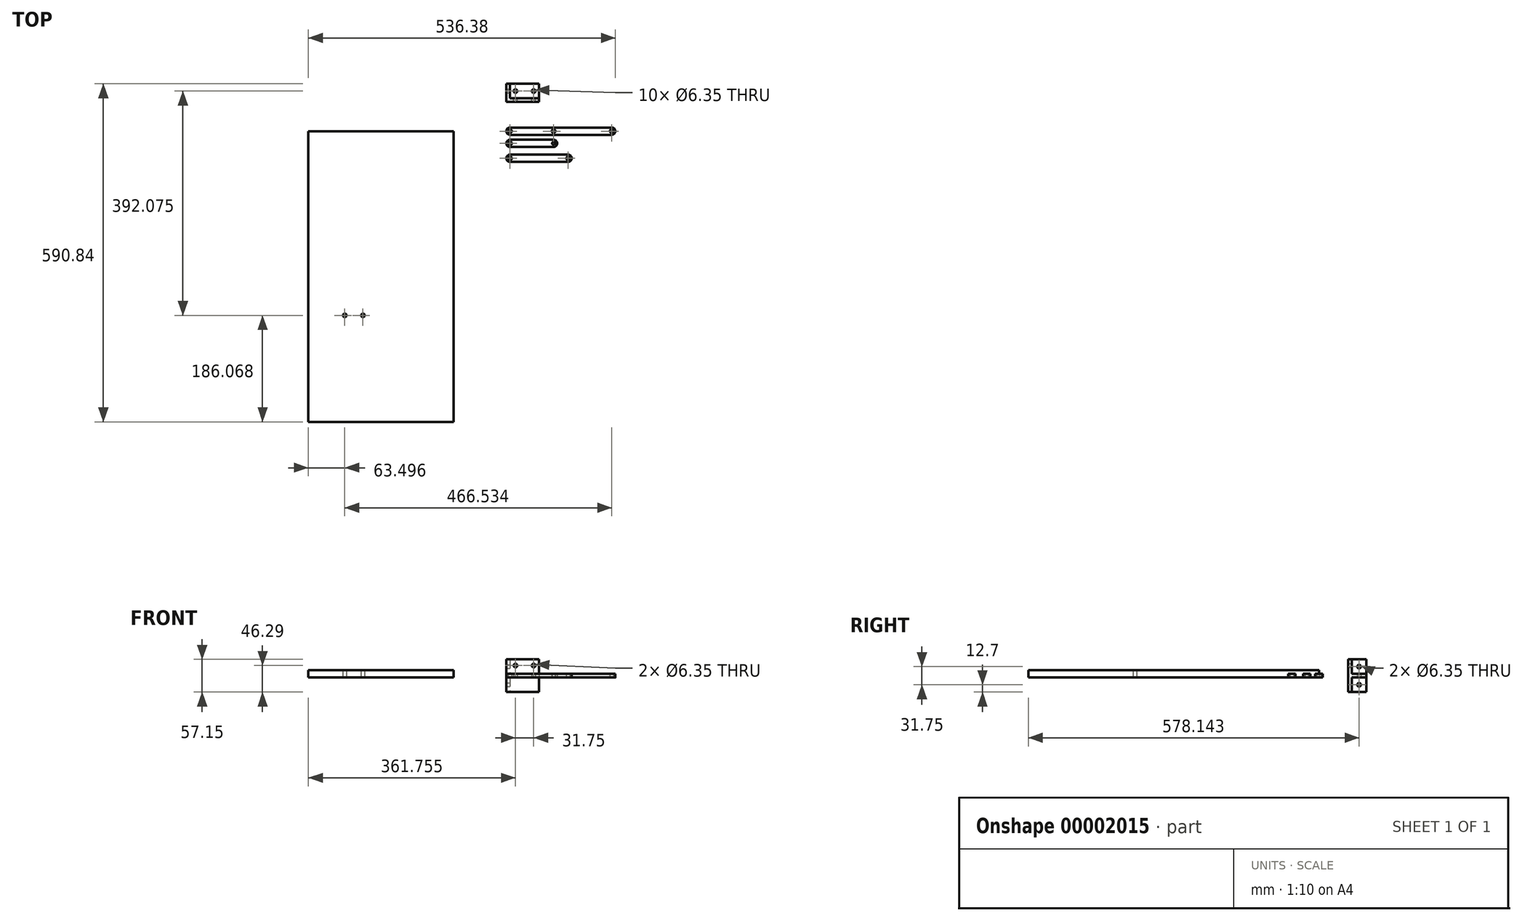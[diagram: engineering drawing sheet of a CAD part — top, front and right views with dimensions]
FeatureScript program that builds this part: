
annotation { "Feature Type Name" : "Feature", "Feature Type Description" : "" }
export const myFeature = defineFeature(function(context is Context, id is Id, definition is map)
    precondition{}
    {
        {
            var Q0;
            Q0=qCreatedBy(makeId("Top.planeOp"),FACE);
            var sketch = newSketch(context, id + "F0", { "sketchPlane" : qUnion([Q0])});
            skCircle(sketch, "E0", {"center": v(0, 0) * mm, "radius": 3.18 * mm});
            skCircle(sketch, "E1", {"center": v(76.2, 0) * mm, "radius": 3.18 * mm});
            skCircle(sketch, "E2", {"center": v(177.8, 0) * mm, "radius": 3.18 * mm});
            skArc(sketch, "E3", {"start": v(0, 6.35) * mm, "mid": v(-6.35, 0) * mm, "end": v(0, -6.35) * mm});
            skArc(sketch, "E4", {"start": v(177.8, -6.35) * mm, "mid": v(184.15, 0) * mm, "end": v(177.8, 6.35) * mm});
            skLineSegment(sketch, "E5", {"start": v(0, -6.35) * mm, "end": v(177.8, -6.35) * mm});
            skLineSegment(sketch, "E6", {"start": v(177.8, 6.35) * mm, "end": v(0, 6.35) * mm});
            skSolve(sketch);
        }
        {
            var Q0;
            Q0=makeQuery(id+"F0.imprint","IMPRINT",FACE,{"disambiguationData":[TD([[makeQuery(id+"F0.imprint","IMPRINT",EDGE,{"derivedFrom":sQuery(id+"F0.wireOp",EDGE,"E0")}),-1.0]])]});
            extrude(context, id + "F1", {"entities" : qUnion([Q0]), "depth" : 6.35 * mm});
        }
        {
            var Q0;
            Q0=qCreatedBy(makeId("Top.planeOp"),FACE);
            var sketch = newSketch(context, id + "F2", { "sketchPlane" : qUnion([Q0])});
            skCircle(sketch, "E7", {"center": v(0, -21.38) * mm, "radius": 3.18 * mm});
            skCircle(sketch, "E8", {"center": v(76.2, -21.38) * mm, "radius": 2.56 * mm});
            skArc(sketch, "E9", {"start": v(0, -15.03) * mm, "mid": v(-6.35, -21.38) * mm, "end": v(0, -27.73) * mm});
            skArc(sketch, "E10", {"start": v(76.2, -27.73) * mm, "mid": v(82.55, -21.38) * mm, "end": v(76.2, -15.03) * mm});
            skLineSegment(sketch, "E11", {"start": v(0, -15.03) * mm, "end": v(76.2, -15.03) * mm});
            skLineSegment(sketch, "E12", {"start": v(76.2, -27.73) * mm, "end": v(0, -27.73) * mm});
            skSolve(sketch);
        }
        {
            var Q0;
            Q0=makeQuery(id+"F2.imprint","IMPRINT",FACE,{"disambiguationData":[TD([[makeQuery(id+"F2.imprint","IMPRINT",EDGE,{"derivedFrom":sQuery(id+"F2.wireOp",EDGE,"E7")}),-1.0]])]});
            extrude(context, id + "F3", {"entities" : qUnion([Q0]), "depth" : 6.35 * mm});
        }
        {
            var Q0;
            Q0=qCreatedBy(makeId("Top.planeOp"),FACE);
            var sketch = newSketch(context, id + "F4", { "sketchPlane" : qUnion([Q0])});
            skLineSegment(sketch, "E13.bottom", {"start": v(0, 82.84) * mm, "end": v(50.8, 82.84) * mm});
            skLineSegment(sketch, "E13.top", {"start": v(0, 57.44) * mm, "end": v(50.8, 57.44) * mm});
            skLineSegment(sketch, "E13.left", {"start": v(0, 82.84) * mm, "end": v(0, 57.44) * mm});
            skLineSegment(sketch, "E13.right", {"start": v(50.8, 82.84) * mm, "end": v(50.8, 57.44) * mm});
            skCircle(sketch, "E14", {"center": v(9.53, 70.14) * mm, "radius": 3.18 * mm});
            skCircle(sketch, "E15", {"center": v(41.28, 70.14) * mm, "radius": 3.18 * mm});
            skSolve(sketch);
        }
        {
            var Q0;
            Q0=makeQuery(id+"F4.imprint","IMPRINT",FACE,{"disambiguationData":[TD([[makeQuery(id+"F4.imprint","IMPRINT",EDGE,{"derivedFrom":sQuery(id+"F4.wireOp",EDGE,"E13.bottom")}),-1.0]])]});
            extrude(context, id + "F5", {"entities" : qUnion([Q0]), "depth" : 6.35 * mm});
        }
        {
            var Q0;
            Q0=makeQuery(id+"F5.opExtrude","SWEPT_FACE",FACE,{"disambiguationData":[OSD([sQuery(id+"F4.wireOp",EDGE,"E13.top")])]});
            var sketch = newSketch(context, id + "F6", { "sketchPlane" : qUnion([Q0])});
            skLineSegment(sketch, "E16.0", {"start": v(0, 6.35) * mm, "end": v(0, 0) * mm});
            skLineSegment(sketch, "E17.0", {"start": v(50.8, 6.35) * mm, "end": v(50.8, 0) * mm});
            skLineSegment(sketch, "E18", {"start": v(0, 6.35) * mm, "end": v(0, 31.75) * mm});
            skLineSegment(sketch, "E19", {"start": v(0, 31.75) * mm, "end": v(50.8, 31.75) * mm});
            skLineSegment(sketch, "E20", {"start": v(50.8, 31.75) * mm, "end": v(50.8, 6.35) * mm});
            skLineSegment(sketch, "E21", {"start": v(0, 0) * mm, "end": v(0, -25.4) * mm});
            skLineSegment(sketch, "E22", {"start": v(0, -25.4) * mm, "end": v(50.8, -25.4) * mm});
            skLineSegment(sketch, "E23", {"start": v(50.8, -25.4) * mm, "end": v(50.8, 0) * mm});
            skLineSegment(sketch, "E24", {"start": v(0, 20.9) * mm, "end": v(50.8, 20.9) * mm, "construction": true});
            skCircle(sketch, "E25", {"center": v(9.53, 20.9) * mm, "radius": 3.18 * mm});
            skCircle(sketch, "E26", {"center": v(41.27, 20.9) * mm, "radius": 3.18 * mm});
            skSolve(sketch);
        }
        {
            var Q0;
            Q0=makeQuery(id+"F6.imprint","IMPRINT",FACE,{"disambiguationData":[TD([[makeQuery(id+"F6.imprint","IMPRINT",EDGE,{"derivedFrom":sQuery(id+"F6.wireOp",EDGE,"E18")}),-1.0]])]});
            var Q1;
            Q1=makeQuery(id+"F6.imprint","IMPRINT",FACE,{"disambiguationData":[TD([[makeQuery(id+"F6.imprint","IMPRINT",EDGE,{"derivedFrom":sQuery(id+"F6.wireOp",EDGE,"E16.0")}),1.0]])]});
            var Q2;
            Q2=makeQuery(id+"F6.imprint","IMPRINT",FACE,{"disambiguationData":[TD([[makeQuery(id+"F6.imprint","IMPRINT",EDGE,{"derivedFrom":sQuery(id+"F6.wireOp",EDGE,"E21")}),1.0]])]});
            extrude(context, id + "F7", {"entities" : qUnion([Q0, Q1, Q2]), "operationType" : NewBodyOperationType.ADD, "depth" : 6.35 * mm});
        }
        {
            var Q0;
            Q0=makeQuery(id+"F7.boolean.opBoolean","MERGE",FACE,{"derivedFrom":[makeQuery(id+"F5.opExtrude","SWEPT_FACE",FACE,{"disambiguationData":[OSD([sQuery(id+"F4.wireOp",EDGE,"E13.left")])]}),makeQuery(id+"F7.opExtrude","SWEPT_FACE",FACE,{"disambiguationData":[OSD([sQuery(id+"F6.wireOp",EDGE,"E16.0"),sQuery(id+"F6.wireOp",EDGE,"E18"),sQuery(id+"F6.wireOp",EDGE,"E21")])]})]});
            var sketch = newSketch(context, id + "F8", { "sketchPlane" : qUnion([Q0])});
            skLineSegment(sketch, "E27.0", {"start": v(-51.1, 31.75) * mm, "end": v(-57.44, 31.75) * mm});
            skLineSegment(sketch, "E28.0", {"start": v(-51.1, -25.4) * mm, "end": v(-57.44, -25.4) * mm});
            skLineSegment(sketch, "E29.0", {"start": v(-82.84, 6.35) * mm, "end": v(-82.84, 0) * mm});
            skLineSegment(sketch, "E30.bottom", {"start": v(-51.1, 31.75) * mm, "end": v(-82.84, 31.75) * mm});
            skLineSegment(sketch, "E30.top", {"start": v(-51.1, -25.4) * mm, "end": v(-82.84, -25.4) * mm});
            skLineSegment(sketch, "E30.left", {"start": v(-51.1, 31.75) * mm, "end": v(-51.1, -25.4) * mm});
            skLineSegment(sketch, "E30.right", {"start": v(-82.84, 31.75) * mm, "end": v(-82.84, -25.4) * mm});
            skCircle(sketch, "E31", {"center": v(-70.14, 19.05) * mm, "radius": 3.18 * mm});
            skCircle(sketch, "E32", {"center": v(-70.14, -12.7) * mm, "radius": 3.18 * mm});
            skSolve(sketch);
        }
        {
            var Q0;
            Q0=makeQuery(id+"F8.imprint","IMPRINT",FACE,{"disambiguationData":[TD([[makeQuery(id+"F8.imprint","IMPRINT",EDGE,{"derivedFrom":sQuery(id+"F8.wireOp",EDGE,"E31")}),-1.0]])]});
            var Q1;
            {var subQ19=sQuery(id+"F8.wireOp",EDGE,"E30.left");Q1=makeQuery(id+"F8.imprint","IMPRINT",FACE,{"disambiguationData":[TD([[makeQuery(id+"F8.imprint","IMPRINT",EDGE,{"derivedFrom":subQ19}),1.0]])]});}
            var Q2;
            Q2=makeQuery(id+"F8.imprint","IMPRINT",FACE,{"disambiguationData":[TD([[makeQuery(id+"F8.imprint","IMPRINT",EDGE,{"derivedFrom":sQuery(id+"F8.wireOp",EDGE,"E32")}),-1.0]])]});
            extrude(context, id + "F9", {"entities" : qUnion([Q0, Q1, Q2]), "operationType" : NewBodyOperationType.ADD, "depth" : 6.35 * mm});
        }
        {
            var Q0;
            Q0=qCreatedBy(makeId("Top.planeOp"),FACE);
            var sketch = newSketch(context, id + "F10", { "sketchPlane" : qUnion([Q0])});
            skLineSegment(sketch, "E33.bottom", {"start": v(-98.23, -508) * mm, "end": v(-352.23, -508) * mm});
            skLineSegment(sketch, "E33.top", {"start": v(-98.23, 0) * mm, "end": v(-352.23, 0) * mm});
            skLineSegment(sketch, "E33.left", {"start": v(-98.23, -508) * mm, "end": v(-98.23, 0) * mm});
            skLineSegment(sketch, "E33.right", {"start": v(-352.23, -508) * mm, "end": v(-352.23, 0) * mm});
            skCircle(sketch, "E34", {"center": v(-288.73, -321.93) * mm, "radius": 3.18 * mm});
            skCircle(sketch, "E35", {"center": v(-256.98, -321.93) * mm, "radius": 3.18 * mm});
            skSolve(sketch);
        }
        {
            var Q0;
            Q0=makeQuery(id+"F10.imprint","IMPRINT",FACE,{"disambiguationData":[TD([[makeQuery(id+"F10.imprint","IMPRINT",EDGE,{"derivedFrom":sQuery(id+"F10.wireOp",EDGE,"E33.bottom")}),-1.0]])]});
            extrude(context, id + "F11", {"entities" : qUnion([Q0]), "depth" : 12.7 * mm});
        }
        {
            var Q0;
            Q0=qCreatedBy(makeId("Top.planeOp"),FACE);
            var sketch = newSketch(context, id + "F12", { "sketchPlane" : qUnion([Q0])});
            skCircle(sketch, "E36", {"center": v(0, -47.4) * mm, "radius": 3.18 * mm});
            skCircle(sketch, "E37", {"center": v(101.6, -47.4) * mm, "radius": 3.18 * mm});
            skArc(sketch, "E38", {"start": v(101.6, -53.76) * mm, "mid": v(107.95, -47.4) * mm, "end": v(101.6, -41.06) * mm});
            skArc(sketch, "E39", {"start": v(0, -41.06) * mm, "mid": v(-6.35, -47.4) * mm, "end": v(0, -53.76) * mm});
            skLineSegment(sketch, "E40", {"start": v(101.6, -53.76) * mm, "end": v(0, -53.76) * mm});
            skLineSegment(sketch, "E41", {"start": v(0, -41.06) * mm, "end": v(101.6, -41.06) * mm});
            skSolve(sketch);
        }
        {
            var Q0;
            Q0=makeQuery(id+"F12.imprint","IMPRINT",FACE,{"disambiguationData":[TD([[makeQuery(id+"F12.imprint","IMPRINT",EDGE,{"derivedFrom":sQuery(id+"F12.wireOp",EDGE,"E36")}),-1.0]])]});
            extrude(context, id + "F13", {"entities" : qUnion([Q0]), "depth" : 6.35 * mm});
        }
    });
